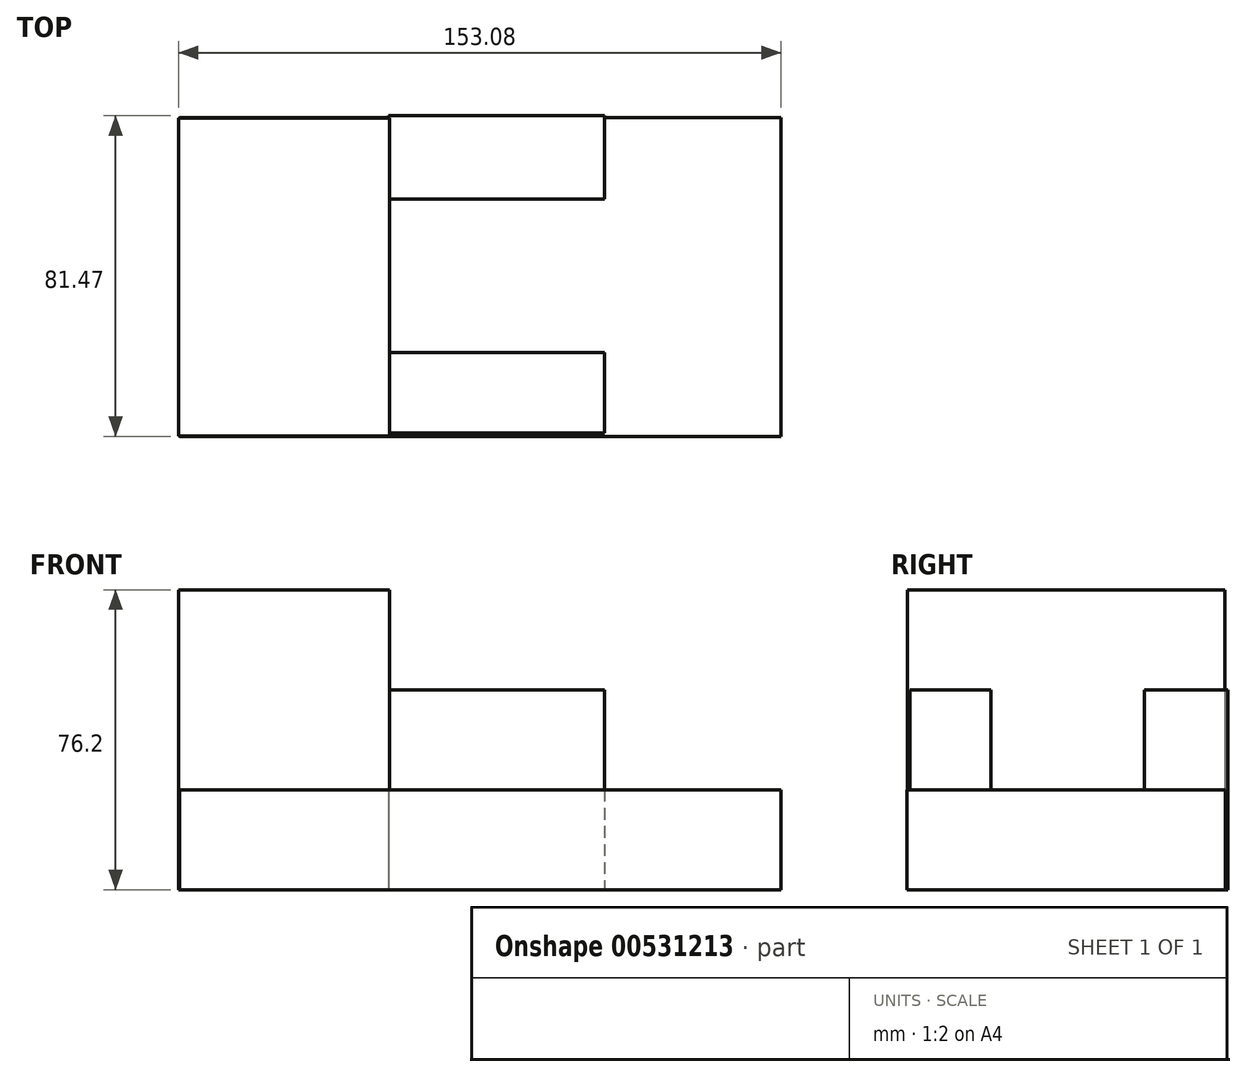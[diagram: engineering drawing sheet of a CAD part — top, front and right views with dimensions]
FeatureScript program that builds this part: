
annotation { "Feature Type Name" : "Feature", "Feature Type Description" : "" }
export const myFeature = defineFeature(function(context is Context, id is Id, definition is map)
    precondition{}
    {
        {
            var Q0;
            Q0=qCreatedBy(makeId("Top.planeOp"),FACE);
            var sketch = newSketch(context, id + "F0", { "sketchPlane" : qUnion([Q0])});
            skLineSegment(sketch, "E0.bottom", {"start": v(-76.38, 40.47) * mm, "end": v(76.38, 40.47) * mm});
            skLineSegment(sketch, "E0.top", {"start": v(-76.38, -40.47) * mm, "end": v(76.38, -40.47) * mm});
            skLineSegment(sketch, "E0.left", {"start": v(-76.38, 40.47) * mm, "end": v(-76.38, -40.47) * mm});
            skLineSegment(sketch, "E0.right", {"start": v(76.38, 40.47) * mm, "end": v(76.38, -40.47) * mm});
            skPoint(sketch, "E0.middle", {"position": v(0, 0) * mm});
            skSolve(sketch);
        }
        {
            var Q0;
            Q0=makeQuery(id+"F0.imprint","IMPRINT",FACE,{"disambiguationData":[TD([[makeQuery(id+"F0.imprint","IMPRINT",EDGE,{"derivedFrom":sQuery(id+"F0.wireOp",EDGE,"E0.bottom")}),-1.0]])]});
            extrude(context, id + "F1", {"entities" : qUnion([Q0]), "depth" : 25.4 * mm, "offsetDistance" : 25.4 * mm});
        }
        {
            var Q0;
            Q0=qCreatedBy(makeId("Top.planeOp"),FACE);
            var sketch = newSketch(context, id + "F2", { "sketchPlane" : qUnion([Q0])});
            skLineSegment(sketch, "E1.bottom", {"start": v(-76.7, 40.34) * mm, "end": v(-23.14, 40.34) * mm});
            skLineSegment(sketch, "E1.top", {"start": v(-76.7, -40.34) * mm, "end": v(-23.14, -40.34) * mm});
            skLineSegment(sketch, "E1.left", {"start": v(-76.7, 40.34) * mm, "end": v(-76.7, -40.34) * mm});
            skLineSegment(sketch, "E1.right", {"start": v(-23.14, 40.34) * mm, "end": v(-23.14, -40.34) * mm});
            skSolve(sketch);
        }
        {
            var Q0;
            Q0 = qSketchRegion(id + "F2", true);
            extrude(context, id + "F3", {"entities" : qUnion([Q0]), "operationType" : NewBodyOperationType.ADD, "depth" : 76.2 * mm, "offsetDistance" : 25.4 * mm});
        }
        {
            var Q0;
            Q0=qCreatedBy(makeId("Top.planeOp"),FACE);
            var sketch = newSketch(context, id + "F4", { "sketchPlane" : qUnion([Q0])});
            skLineSegment(sketch, "E2.bottom", {"start": v(-23.3, -39.67) * mm, "end": v(31.58, -39.67) * mm});
            skLineSegment(sketch, "E2.top", {"start": v(-23.3, -19.18) * mm, "end": v(31.58, -19.18) * mm});
            skLineSegment(sketch, "E2.left", {"start": v(-23.3, -39.67) * mm, "end": v(-23.3, -19.18) * mm});
            skLineSegment(sketch, "E2.right", {"start": v(31.58, -39.67) * mm, "end": v(31.58, -19.18) * mm});
            skLineSegment(sketch, "E3.bottom", {"start": v(-23.3, 41) * mm, "end": v(31.58, 41) * mm});
            skLineSegment(sketch, "E3.top", {"start": v(-23.3, 19.84) * mm, "end": v(31.58, 19.84) * mm});
            skLineSegment(sketch, "E3.left", {"start": v(-23.3, 41) * mm, "end": v(-23.3, 19.84) * mm});
            skLineSegment(sketch, "E3.right", {"start": v(31.58, 41) * mm, "end": v(31.58, 19.84) * mm});
            skSolve(sketch);
        }
        {
            var Q0;
            Q0 = qSketchRegion(id + "F4", true);
            extrude(context, id + "F5", {"entities" : qUnion([Q0]), "operationType" : NewBodyOperationType.ADD, "depth" : 50.8 * mm, "offsetDistance" : 25.4 * mm});
        }
    });
